# Revit family: R1200-JD-W31P24L-F1444
name_source: partatom
category: Plumbing Fixtures
revit_build: Autodesk Revit 2018 (Build: 20170223_1515(x64)
units: mm (PartAtom-declared; Revit-internal decimal feet)

## family parameters
Cut with Voids When Loaded = No
Host = Face
Part Type = Normal
Room Calculation Point = No
Round Connector Dimension = Use Radius
Shared = No

## types (6) — shared parameters
Bottom Height = 0' - 3 1/2"
Default Elevation = 0' - 0"
Description = LARGE GREEN PROMENADE ROOF DRAIN WITH PERFORATED PVC STANDPIPE, STAINLESS STEEL MESH COVERED CAST IRON DOME AND TOP 12" X 12" DUCTILE IRON STRAINER
Floor Drain Material = Paint - Sherwin Williams Paint - #952C2A - Bellwood Red
Manufacturer = MIFAB
URL = WWW.MIFAB.COM
zero-valued in all types: CWFU, WFU

## per-type parameters (varying)
| type | Model | No Hub Standard Height | Pipe Diameter | Pipe Radius |
| R1205,6-JD-W31P24L-F1444-6" Drain Pipe Size | R1205,6-JD-W31P24L-F1444 | 0' - 6 1/2" | 0' - 6" | 0' - 3" |
| R1208-JD-W31P24L-F1444-8" Drain Pipe Size | R1208-JD-W31P24L-F1444 | 0' - 6 1/2" | 0' - 8" | 0' - 4" |
| R1205,6-JD-W31P24L-F1444 -5" Drain Pipe Size | R1205,6-JD-W31P24L-F1444 | 0' - 6 3/4" | 0' - 5" | 0' - 2 1/2" |
| R1202,3,4-JD-W31P24L-F1444 -4" Drain Pipe Size | R1202,3,4-JD-W31P24L-F1444 | 0' - 6 1/2" | 0' - 4" | 0' - 2" |
| R1202,3,4-JD-W31P24L-F1444-3" Drain Pipe Size | R1202,3,4-JD-W31P24L-F1444 | 0' - 6 7/16" | 0' - 3" | 0' - 1 1/2" |
| R1202,3,4-JD-W31P24L-F1444 -2" Drain Pipe Size | R1202,3,4-JD-W31P24L-F1444 | 0' - 6 1/2" | 0' - 2" | 0' - 1" |

## geometry (parser evidence)
native form markers: Sweep x13
no freeform markers — native parametric forms only
